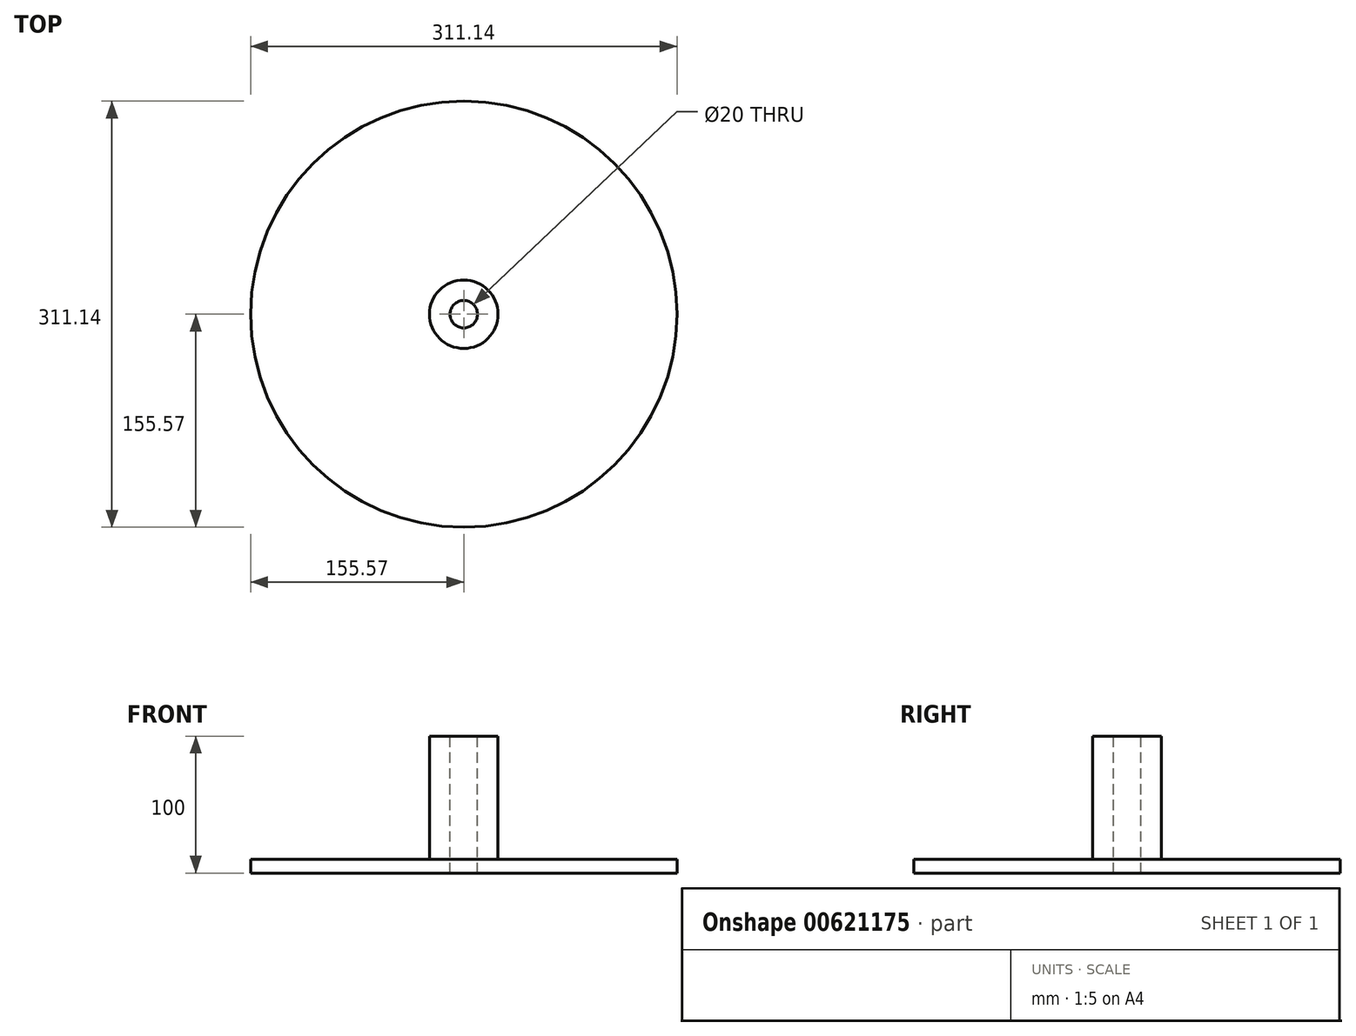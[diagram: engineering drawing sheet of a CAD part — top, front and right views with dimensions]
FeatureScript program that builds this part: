
annotation { "Feature Type Name" : "Feature", "Feature Type Description" : "" }
export const myFeature = defineFeature(function(context is Context, id is Id, definition is map)
    precondition{}
    {
        {
            var Q0;
            Q0=qCreatedBy(makeId("Right.planeOp"),FACE);
            var sketch = newSketch(context, id + "F0", { "sketchPlane" : qUnion([Q0])});
            skLineSegment(sketch, "E0", {"start": v(10, 148.9) * mm, "end": v(10, -150.56) * mm, "construction": true});
            skLineSegment(sketch, "E1", {"start": v(0, 0) * mm, "end": v(-145.57, 0) * mm});
            skLineSegment(sketch, "E2", {"start": v(-145.57, 0) * mm, "end": v(-145.57, 10) * mm});
            skLineSegment(sketch, "E3", {"start": v(-145.57, 10) * mm, "end": v(-15, 10) * mm});
            skLineSegment(sketch, "E4", {"start": v(-15, 10) * mm, "end": v(-15, 100) * mm});
            skLineSegment(sketch, "E5", {"start": v(-15, 100) * mm, "end": v(0, 100) * mm});
            skLineSegment(sketch, "E6", {"start": v(0, 100) * mm, "end": v(0, 0) * mm});
            skSolve(sketch);
        }
        {
            var Q0;
            Q0 = qSketchRegion(id + "F0", true);
            var Q1;
            Q1=sQuery(id+"F0.wireOp",EDGE,"E0");
            revolve(context, id + "F1", {"entities" : qUnion([Q0]), "axis" : qUnion([Q1]), "revolveType" : RevolveType.FULL});
        }
        {
            var Q0;
            Q0=qCreatedBy(makeId("Front.planeOp"),FACE);
            cPlane(context, id + "F2", {"entities" : qUnion([Q0]), "cplaneType" : CPlaneType.OFFSET, "offset" : 10 * mm, "oppositeDirection" : true, "width" : 150 * mm, "height" : 150 * mm});
        }
    });
